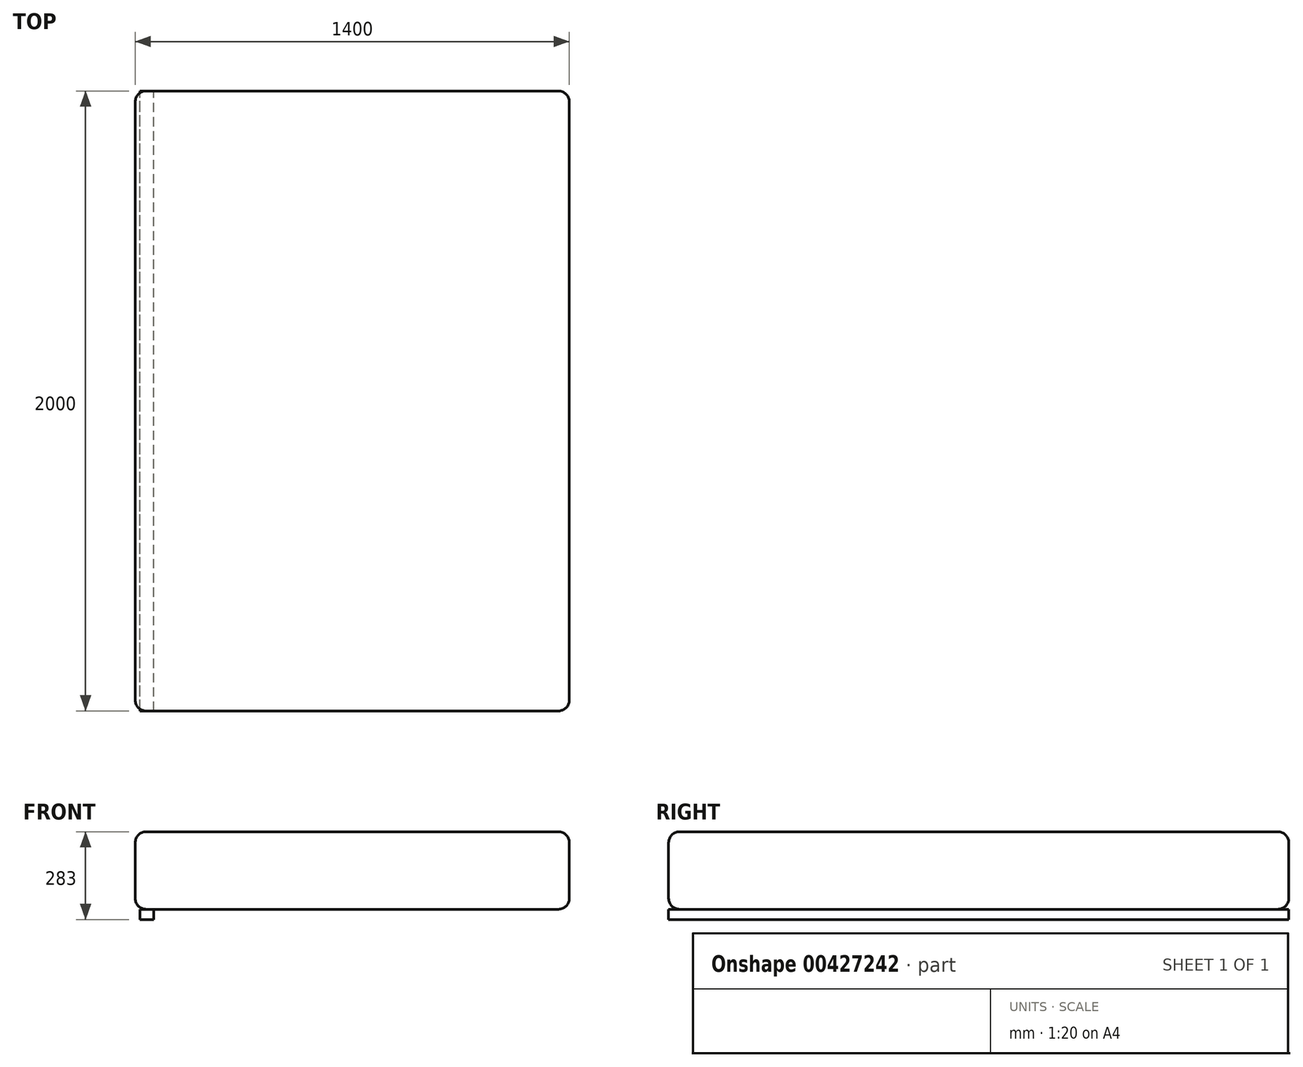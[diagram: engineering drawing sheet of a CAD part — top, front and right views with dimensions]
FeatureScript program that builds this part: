
annotation { "Feature Type Name" : "Feature", "Feature Type Description" : "" }
export const myFeature = defineFeature(function(context is Context, id is Id, definition is map)
    precondition{}
    {
        {
            var Q0;
            Q0=qCreatedBy(makeId("Top.planeOp"),FACE);
            var sketch = newSketch(context, id + "F0", { "sketchPlane" : qUnion([Q0])});
            skLineSegment(sketch, "E0.bottom", {"start": v(700, 1000) * mm, "end": v(-700, 1000) * mm});
            skLineSegment(sketch, "E0.top", {"start": v(700, -1000) * mm, "end": v(-700, -1000) * mm});
            skLineSegment(sketch, "E0.left", {"start": v(700, 1000) * mm, "end": v(700, -1000) * mm});
            skLineSegment(sketch, "E0.right", {"start": v(-700, 1000) * mm, "end": v(-700, -1000) * mm});
            skPoint(sketch, "E0.middle", {"position": v(0, 0) * mm});
            skSolve(sketch);
        }
        {
            var Q0;
            Q0=makeQuery(id+"F0.imprint","IMPRINT",FACE,{"disambiguationData":[TD([[makeQuery(id+"F0.imprint","IMPRINT",EDGE,{"derivedFrom":sQuery(id+"F0.wireOp",EDGE,"E0.bottom")}),1.0]])]});
            extrude(context, id + "F1", {"entities" : qUnion([Q0]), "depth" : 250 * mm});
        }
        {
            var Q0;
            Q0=makeQuery(id+"F1.opExtrude","CAP_EDGE",EDGE,{"disambiguationData":[OSD([sQuery(id+"F0.wireOp",EDGE,"E0.right")])],"isStart":false});
            var Q1;
            Q1=makeQuery(id+"F1.opExtrude","CAP_EDGE",EDGE,{"disambiguationData":[OSD([sQuery(id+"F0.wireOp",EDGE,"E0.top")])],"isStart":false});
            var Q2;
            Q2=makeQuery(id+"F1.opExtrude","SWEPT_EDGE",EDGE,{"disambiguationData":[OSD([sQuery(id+"F0.wireOp",EDGE,"E0.top"),sQuery(id+"F0.wireOp",EDGE,"E0.right")])]});
            var Q3;
            Q3=makeQuery(id+"F1.opExtrude","CAP_EDGE",EDGE,{"disambiguationData":[OSD([sQuery(id+"F0.wireOp",EDGE,"E0.left")])],"isStart":false});
            var Q4;
            Q4=makeQuery(id+"F1.opExtrude","CAP_EDGE",EDGE,{"disambiguationData":[OSD([sQuery(id+"F0.wireOp",EDGE,"E0.bottom")])],"isStart":false});
            var Q5;
            Q5=makeQuery(id+"F1.opExtrude","SWEPT_EDGE",EDGE,{"disambiguationData":[OSD([sQuery(id+"F0.wireOp",EDGE,"E0.top"),sQuery(id+"F0.wireOp",EDGE,"E0.left")])]});
            var Q6;
            Q6=makeQuery(id+"F1.opExtrude","CAP_EDGE",EDGE,{"disambiguationData":[OSD([sQuery(id+"F0.wireOp",EDGE,"E0.top")])],"isStart":true});
            var Q7;
            Q7=makeQuery(id+"F1.opExtrude","CAP_EDGE",EDGE,{"disambiguationData":[OSD([sQuery(id+"F0.wireOp",EDGE,"E0.left")])],"isStart":true});
            var Q8;
            Q8=makeQuery(id+"F1.opExtrude","SWEPT_EDGE",EDGE,{"disambiguationData":[OSD([sQuery(id+"F0.wireOp",EDGE,"E0.bottom"),sQuery(id+"F0.wireOp",EDGE,"E0.right")])]});
            var Q9;
            Q9=makeQuery(id+"F1.opExtrude","CAP_EDGE",EDGE,{"disambiguationData":[OSD([sQuery(id+"F0.wireOp",EDGE,"E0.bottom")])],"isStart":true});
            var Q10;
            Q10=makeQuery(id+"F1.opExtrude","SWEPT_EDGE",EDGE,{"disambiguationData":[OSD([sQuery(id+"F0.wireOp",EDGE,"E0.bottom"),sQuery(id+"F0.wireOp",EDGE,"E0.left")])]});
            var Q11;
            Q11=makeQuery(id+"F1.opExtrude","CAP_EDGE",EDGE,{"disambiguationData":[OSD([sQuery(id+"F0.wireOp",EDGE,"E0.right")])],"isStart":true});
            fillet(context, id + "F2", {"entities" : qUnion([Q0, Q1, Q2, Q3, Q4, Q5, Q6, Q7, Q8, Q9, Q10, Q11]), "radius" : 35 * mm, "tangentPropagation" : true, "allowEdgeOverflow" : false});
        }
        {
            var Q0;
            Q0=qCreatedBy(makeId("Front.planeOp"),FACE);
            var sketch = newSketch(context, id + "F3", { "sketchPlane" : qUnion([Q0])});
            skLineSegment(sketch, "E1.bottom", {"start": v(-685, 0) * mm, "end": v(-640, 0) * mm});
            skLineSegment(sketch, "E1.top", {"start": v(-685, -33) * mm, "end": v(-640, -33) * mm});
            skLineSegment(sketch, "E1.left", {"start": v(-685, 0) * mm, "end": v(-685, -33) * mm});
            skLineSegment(sketch, "E1.right", {"start": v(-640, 0) * mm, "end": v(-640, -33) * mm});
            skSolve(sketch);
        }
        {
            var Q0;
            Q0=makeQuery(id+"F3.imprint","IMPRINT",FACE,{"disambiguationData":[TD([[makeQuery(id+"F3.imprint","IMPRINT",EDGE,{"derivedFrom":sQuery(id+"F3.wireOp",EDGE,"E1.bottom")}),-1.0]])]});
            extrude(context, id + "F4", {"entities" : qUnion([Q0]), "endBound" : BoundingType.SYMMETRIC, "depth" : 2000 * mm});
        }
    });
